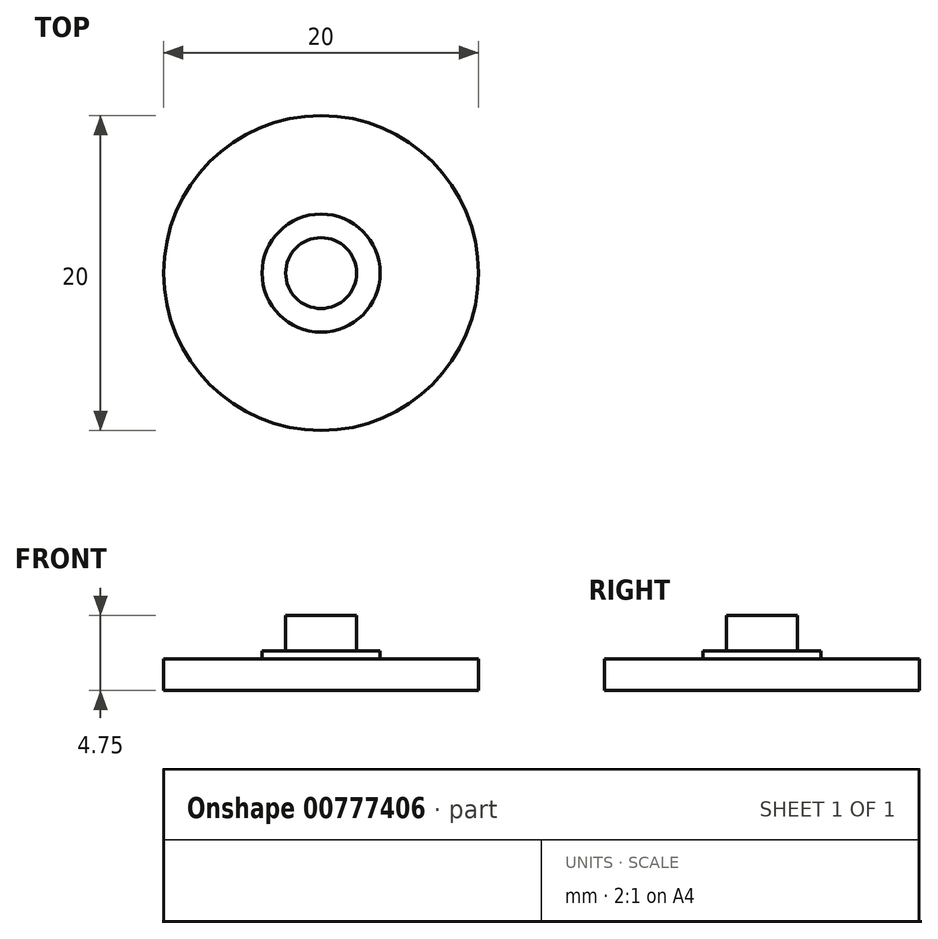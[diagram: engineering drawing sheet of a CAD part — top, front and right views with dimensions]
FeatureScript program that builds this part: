
annotation { "Feature Type Name" : "Feature", "Feature Type Description" : "" }
export const myFeature = defineFeature(function(context is Context, id is Id, definition is map)
    precondition{}
    {
        {
            var Q0;
            Q0=qCreatedBy(makeId("Top.planeOp"),FACE);
            var sketch = newSketch(context, id + "F0", { "sketchPlane" : qUnion([Q0])});
            skCircle(sketch, "E0", {"center": v(0, 0) * mm, "radius": 10 * mm});
            skCircle(sketch, "E1", {"center": v(0, 0) * mm, "radius": 2.25 * mm});
            skCircle(sketch, "E2", {"center": v(0, 0) * mm, "radius": 3.75 * mm});
            skSolve(sketch);
        }
        {
            var Q0;
            Q0=makeQuery(id+"F0.imprint","IMPRINT",FACE,{"disambiguationData":[TD([[makeQuery(id+"F0.imprint","IMPRINT",EDGE,{"derivedFrom":sQuery(id+"F0.wireOp",EDGE,"E0")}),1.0]])]});
            var Q1;
            Q1=makeQuery(id+"F0.imprint","IMPRINT",FACE,{"disambiguationData":[TD([[makeQuery(id+"F0.imprint","IMPRINT",EDGE,{"derivedFrom":sQuery(id+"F0.wireOp",EDGE,"E1")}),-1.0]])]});
            extrude(context, id + "F1", {"entities" : qUnion([Q0, Q1]), "depth" : 2 * mm, "offsetDistance" : 25 * mm});
        }
        {
            var Q0;
            Q0=makeQuery(id+"F0.imprint","IMPRINT",FACE,{"disambiguationData":[TD([[makeQuery(id+"F0.imprint","IMPRINT",EDGE,{"derivedFrom":sQuery(id+"F0.wireOp",EDGE,"E1")}),1.0]])]});
            extrude(context, id + "F2", {"entities" : qUnion([Q0]), "operationType" : NewBodyOperationType.ADD, "depth" : 4.75 * mm, "offsetDistance" : 25 * mm});
        }
        {
            var Q0;
            Q0=makeQuery(id+"F0.imprint","IMPRINT",FACE,{"disambiguationData":[TD([[makeQuery(id+"F0.imprint","IMPRINT",EDGE,{"derivedFrom":sQuery(id+"F0.wireOp",EDGE,"E1")}),-1.0]])]});
            extrude(context, id + "F3", {"entities" : qUnion([Q0]), "operationType" : NewBodyOperationType.ADD, "depth" : 2.5 * mm, "offsetDistance" : 25 * mm});
        }
    });
